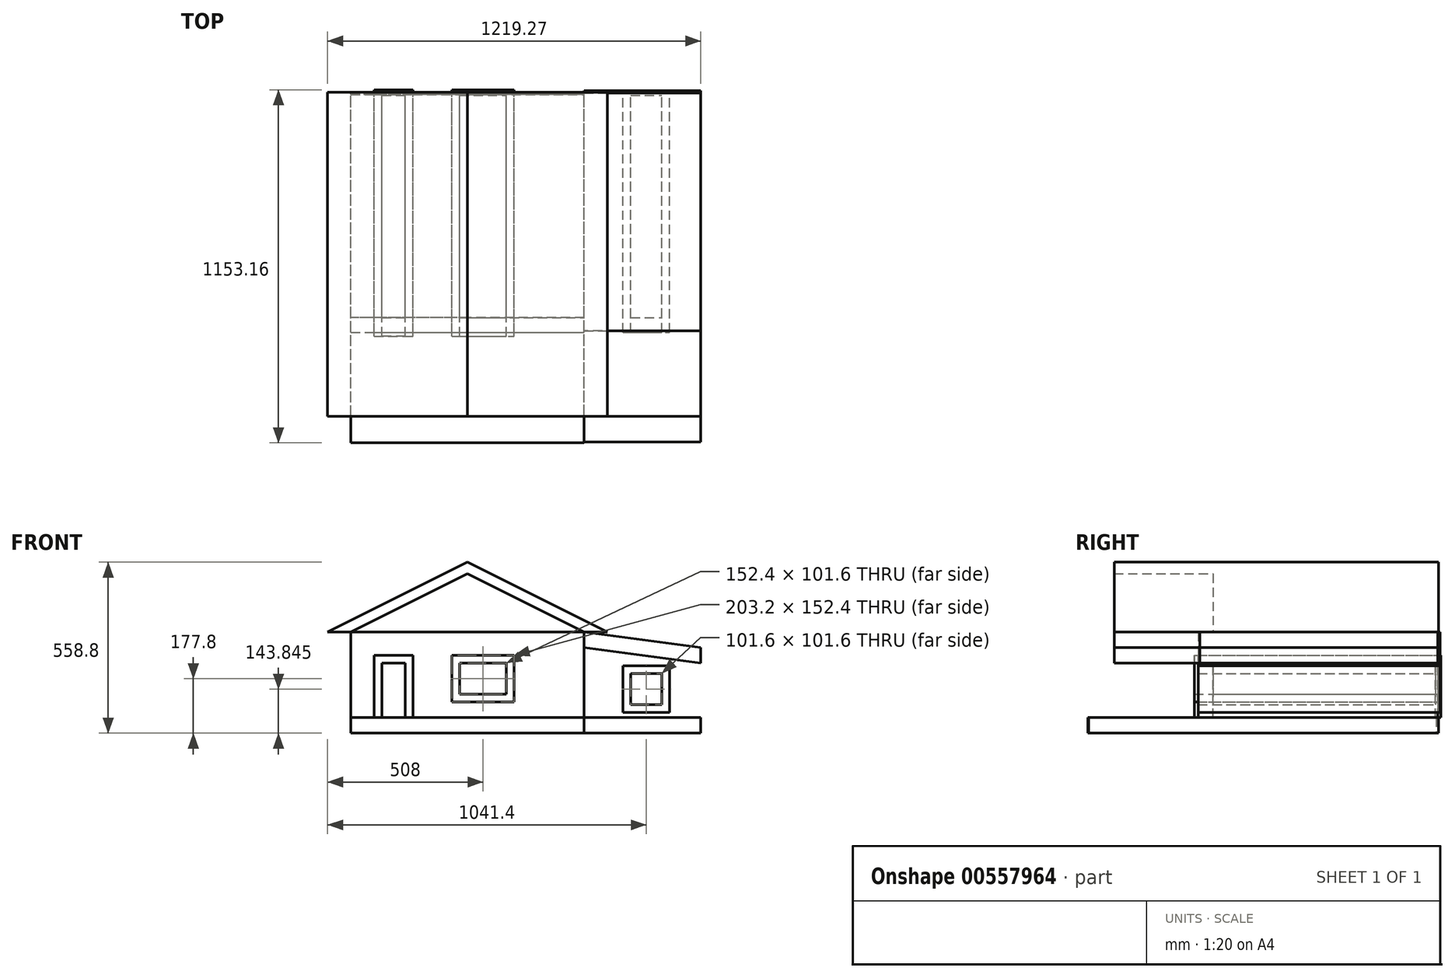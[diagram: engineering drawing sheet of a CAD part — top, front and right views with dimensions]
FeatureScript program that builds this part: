
annotation { "Feature Type Name" : "Feature", "Feature Type Description" : "" }
export const myFeature = defineFeature(function(context is Context, id is Id, definition is map)
    precondition{}
    {
        {
            var Q0;
            Q0=qCreatedBy(makeId("Front.planeOp"),FACE);
            var sketch = newSketch(context, id + "F0", { "sketchPlane" : qUnion([Q0])});
            skLineSegment(sketch, "E0", {"start": v(0, 0) * mm, "end": v(-381, 0) * mm});
            skLineSegment(sketch, "E1", {"start": v(0, 0) * mm, "end": v(381, 0) * mm});
            skLineSegment(sketch, "E2", {"start": v(0, 0) * mm, "end": v(0, 190.5) * mm});
            skLineSegment(sketch, "E3", {"start": v(0, 190.5) * mm, "end": v(-381, 0) * mm});
            skLineSegment(sketch, "E4", {"start": v(0, 190.5) * mm, "end": v(381, 0) * mm});
            skLineSegment(sketch, "E5", {"start": v(-381, 0) * mm, "end": v(-381, -279.4) * mm});
            skLineSegment(sketch, "E6", {"start": v(381, 0) * mm, "end": v(381, -279.4) * mm});
            skLineSegment(sketch, "E7", {"start": v(-381, -279.4) * mm, "end": v(381, -279.4) * mm});
            skLineSegment(sketch, "E8", {"start": v(0, 190.5) * mm, "end": v(0, 228.6) * mm});
            skLineSegment(sketch, "E9", {"start": v(-381, 0) * mm, "end": v(-457.2, 0) * mm});
            skLineSegment(sketch, "E10", {"start": v(381, 0) * mm, "end": v(457.2, 0) * mm});
            skLineSegment(sketch, "E11", {"start": v(457.2, 0) * mm, "end": v(0, 228.6) * mm});
            skLineSegment(sketch, "E12", {"start": v(0, 228.6) * mm, "end": v(-457.2, 0) * mm});
            skLineSegment(sketch, "E13", {"start": v(381, 0) * mm, "end": v(762, -50.27) * mm});
            skLineSegment(sketch, "E14", {"start": v(762, -50.27) * mm, "end": v(762, -278.87) * mm});
            skLineSegment(sketch, "E15", {"start": v(762, -278.87) * mm, "end": v(381, -279.4) * mm});
            skLineSegment(sketch, "E16", {"start": v(381, 0) * mm, "end": v(381, -50.8) * mm});
            skLineSegment(sketch, "E17", {"start": v(762, -50.27) * mm, "end": v(762, -101.07) * mm});
            skLineSegment(sketch, "E18", {"start": v(762, -101.07) * mm, "end": v(381, -50.8) * mm});
            skLineSegment(sketch, "E19", {"start": v(-381, -279.4) * mm, "end": v(-381, -330.2) * mm});
            skLineSegment(sketch, "E20", {"start": v(762, -278.87) * mm, "end": v(762.07, -329.67) * mm});
            skLineSegment(sketch, "E21", {"start": v(762.07, -329.67) * mm, "end": v(-381, -330.2) * mm});
            skLineSegment(sketch, "E22", {"start": v(-279.4, -279.4) * mm, "end": v(-279.4, -101.6) * mm});
            skLineSegment(sketch, "E23", {"start": v(-203.2, -101.6) * mm, "end": v(-279.4, -101.6) * mm});
            skLineSegment(sketch, "E24", {"start": v(-203.2, -101.6) * mm, "end": v(-203.2, -279.4) * mm});
            skLineSegment(sketch, "E25", {"start": v(-279.4, -279.4) * mm, "end": v(-304.8, -279.4) * mm});
            skLineSegment(sketch, "E26", {"start": v(-304.8, -279.4) * mm, "end": v(-304.9, -76.26) * mm});
            skLineSegment(sketch, "E27", {"start": v(-304.9, -76.26) * mm, "end": v(-177.8, -76.2) * mm});
            skLineSegment(sketch, "E28", {"start": v(-177.8, -76.2) * mm, "end": v(-177.8, -279.4) * mm});
            skLineSegment(sketch, "E29", {"start": v(-203.2, -279.4) * mm, "end": v(-177.8, -279.4) * mm});
            skLineSegment(sketch, "E30", {"start": v(381, -279.4) * mm, "end": v(381.07, -329.85) * mm});
            skLineSegment(sketch, "E31.bottom", {"start": v(-25.4, -101.6) * mm, "end": v(127, -101.6) * mm});
            skLineSegment(sketch, "E31.top", {"start": v(-25.4, -203.2) * mm, "end": v(127, -203.2) * mm});
            skLineSegment(sketch, "E31.left", {"start": v(-25.4, -101.6) * mm, "end": v(-25.4, -203.2) * mm});
            skLineSegment(sketch, "E31.right", {"start": v(127, -101.6) * mm, "end": v(127, -203.2) * mm});
            skLineSegment(sketch, "E32.bottom", {"start": v(533.4, -135.56) * mm, "end": v(635, -135.56) * mm});
            skLineSegment(sketch, "E32.top", {"start": v(533.4, -237.16) * mm, "end": v(635, -237.16) * mm});
            skLineSegment(sketch, "E32.left", {"start": v(533.4, -135.56) * mm, "end": v(533.4, -237.16) * mm});
            skLineSegment(sketch, "E32.right", {"start": v(635, -135.56) * mm, "end": v(635, -237.16) * mm});
            skLineSegment(sketch, "E33.0", {"start": v(-50.8, -76.2) * mm, "end": v(152.4, -76.2) * mm});
            skLineSegment(sketch, "E33.1", {"start": v(-50.8, -76.2) * mm, "end": v(-50.8, -228.6) * mm});
            skLineSegment(sketch, "E33.2", {"start": v(-50.8, -228.6) * mm, "end": v(152.4, -228.6) * mm});
            skLineSegment(sketch, "E33.3", {"start": v(152.4, -76.2) * mm, "end": v(152.4, -228.6) * mm});
            skLineSegment(sketch, "E34.0", {"start": v(508, -110.16) * mm, "end": v(508, -262.56) * mm});
            skLineSegment(sketch, "E34.1", {"start": v(508, -110.16) * mm, "end": v(660.4, -110.16) * mm});
            skLineSegment(sketch, "E34.2", {"start": v(660.4, -110.16) * mm, "end": v(660.4, -262.56) * mm});
            skLineSegment(sketch, "E34.3", {"start": v(508, -262.56) * mm, "end": v(660.4, -262.56) * mm});
            skSolve(sketch);
        }
        {
            var Q0;
            Q0=makeQuery(id+"F0.imprint","IMPRINT",FACE,{"disambiguationData":[TD([[makeQuery(id+"F0.imprint","IMPRINT",EDGE,{"derivedFrom":sQuery(id+"F0.wireOp",EDGE,"E3")}),-1.0]])]});
            var Q1;
            Q1=makeQuery(id+"F0.imprint","IMPRINT",FACE,{"disambiguationData":[TD([[makeQuery(id+"F0.imprint","IMPRINT",EDGE,{"derivedFrom":sQuery(id+"F0.wireOp",EDGE,"E4")}),1.0]])]});
            extrude(context, id + "F1", {"entities" : qUnion([Q0, Q1]), "depth" : 596.9 * mm, "offsetDistance" : 25.4 * mm, "hasSecondDirection" : true, "secondDirectionOppositeDirection" : true, "secondDirectionDepth" : 462.28 * mm});
        }
        {
            var Q0;
            Q0=makeQuery(id+"F0.imprint","IMPRINT",FACE,{"disambiguationData":[TD([[makeQuery(id+"F0.imprint","IMPRINT",EDGE,{"derivedFrom":sQuery(id+"F0.wireOp",EDGE,"E0")}),-1.0]])]});
            var Q1;
            Q1=makeQuery(id+"F0.imprint","IMPRINT",FACE,{"disambiguationData":[TD([[makeQuery(id+"F0.imprint","IMPRINT",EDGE,{"derivedFrom":sQuery(id+"F0.wireOp",EDGE,"E1")}),1.0]])]});
            extrude(context, id + "F2", {"entities" : qUnion([Q0, Q1]), "operationType" : NewBodyOperationType.ADD, "depth" : 274.32 * mm, "offsetDistance" : 25.4 * mm, "hasSecondDirection" : true, "secondDirectionOppositeDirection" : true, "secondDirectionDepth" : 462.28 * mm});
        }
        {
            var Q0;
            Q0=makeQuery(id+"F0.imprint","IMPRINT",FACE,{"disambiguationData":[TD([[makeQuery(id+"F0.imprint","IMPRINT",EDGE,{"derivedFrom":sQuery(id+"F0.wireOp",EDGE,"E13")}),-1.0]])]});
            extrude(context, id + "F3", {"entities" : qUnion([Q0]), "depth" : 596.9 * mm, "offsetDistance" : 25.4 * mm, "hasSecondDirection" : true, "secondDirectionOppositeDirection" : true, "secondDirectionDepth" : 467.36 * mm});
        }
        {
            var Q0;
            Q0=makeQuery(id+"F0.imprint","IMPRINT",FACE,{"disambiguationData":[TD([[makeQuery(id+"F0.imprint","IMPRINT",EDGE,{"derivedFrom":sQuery(id+"F0.wireOp",EDGE,"E0")}),1.0]])]});
            extrude(context, id + "F4", {"entities" : qUnion([Q0]), "depth" : 322.58 * mm, "offsetDistance" : 25.4 * mm, "hasSecondDirection" : true, "secondDirectionOppositeDirection" : true, "secondDirectionDepth" : 459.74 * mm});
        }
        {
            var Q0;
            {var subQ0=sQuery(id+"F0.wireOp",EDGE,"E19");Q0=makeQuery(id+"F0.imprint","IMPRINT",FACE,{"disambiguationData":[TD([[makeQuery(id+"F0.imprint","IMPRINT",EDGE,{"derivedFrom":subQ0}),1.0]])]});}
            extrude(context, id + "F5", {"entities" : qUnion([Q0]), "operationType" : NewBodyOperationType.ADD, "depth" : 683.26 * mm, "offsetDistance" : 25.4 * mm, "hasSecondDirection" : true, "secondDirectionOppositeDirection" : true, "secondDirectionDepth" : 454.66 * mm});
        }
        {
            var Q0;
            {var subQ0=sQuery(id+"F0.wireOp",EDGE,"E22");Q0=makeQuery(id+"F0.imprint","IMPRINT",FACE,{"disambiguationData":[TD([[makeQuery(id+"F0.imprint","IMPRINT",EDGE,{"derivedFrom":subQ0}),-1.0]])]});}
            var Q1;
            Q1=makeQuery(id+"F0.imprint","IMPRINT",FACE,{"disambiguationData":[TD([[makeQuery(id+"F0.imprint","IMPRINT",EDGE,{"derivedFrom":sQuery(id+"F0.wireOp",EDGE,"E31.bottom")}),-1.0]])]});
            var Q2;
            Q2=makeQuery(id+"F0.imprint","IMPRINT",FACE,{"disambiguationData":[TD([[makeQuery(id+"F0.imprint","IMPRINT",EDGE,{"derivedFrom":sQuery(id+"F0.wireOp",EDGE,"E32.bottom")}),-1.0]])]});
            extrude(context, id + "F6", {"entities" : qUnion([Q0, Q1, Q2]), "operationType" : NewBodyOperationType.ADD, "depth" : 274.32 * mm, "offsetDistance" : 25.4 * mm, "hasSecondDirection" : true, "secondDirectionOppositeDirection" : true, "secondDirectionDepth" : 452.12 * mm});
        }
        {
            var Q0;
            Q0=makeQuery(id+"F0.imprint","IMPRINT",FACE,{"disambiguationData":[TD([[makeQuery(id+"F0.imprint","IMPRINT",EDGE,{"derivedFrom":sQuery(id+"F0.wireOp",EDGE,"E22")}),1.0]])]});
            var Q1;
            Q1=makeQuery(id+"F0.imprint","IMPRINT",FACE,{"disambiguationData":[TD([[makeQuery(id+"F0.imprint","IMPRINT",EDGE,{"derivedFrom":sQuery(id+"F0.wireOp",EDGE,"E31.bottom")}),1.0]])]});
            extrude(context, id + "F7", {"entities" : qUnion([Q0, Q1]), "depth" : 335.28 * mm, "offsetDistance" : 25.4 * mm, "hasSecondDirection" : true, "secondDirectionOppositeDirection" : true, "secondDirectionDepth" : 469.9 * mm});
        }
        {
            var Q0;
            Q0=makeQuery(id+"F0.imprint","IMPRINT",FACE,{"disambiguationData":[TD([[makeQuery(id+"F0.imprint","IMPRINT",EDGE,{"derivedFrom":sQuery(id+"F0.wireOp",EDGE,"E6")}),1.0]])]});
            extrude(context, id + "F8", {"entities" : qUnion([Q0]), "depth" : 317.5 * mm, "offsetDistance" : 25.4 * mm, "hasSecondDirection" : true, "secondDirectionOppositeDirection" : true, "secondDirectionDepth" : 459.74 * mm});
        }
        {
            var Q0;
            Q0=makeQuery(id+"F0.imprint","IMPRINT",FACE,{"disambiguationData":[TD([[makeQuery(id+"F0.imprint","IMPRINT",EDGE,{"derivedFrom":sQuery(id+"F0.wireOp",EDGE,"E32.bottom")}),1.0]])]});
            extrude(context, id + "F9", {"entities" : qUnion([Q0]), "depth" : 322.58 * mm, "offsetDistance" : 25.4 * mm, "hasSecondDirection" : true, "secondDirectionOppositeDirection" : true, "secondDirectionDepth" : 467.36 * mm});
        }
        {
            var Q0;
            Q0=makeQuery(id+"F0.imprint","IMPRINT",FACE,{"disambiguationData":[TD([[makeQuery(id+"F0.imprint","IMPRINT",EDGE,{"derivedFrom":sQuery(id+"F0.wireOp",EDGE,"E15")}),1.0]])]});
            extrude(context, id + "F10", {"entities" : qUnion([Q0]), "depth" : 680.72 * mm, "offsetDistance" : 25.4 * mm, "hasSecondDirection" : true, "secondDirectionOppositeDirection" : true, "secondDirectionDepth" : 462.28 * mm});
        }
    });
